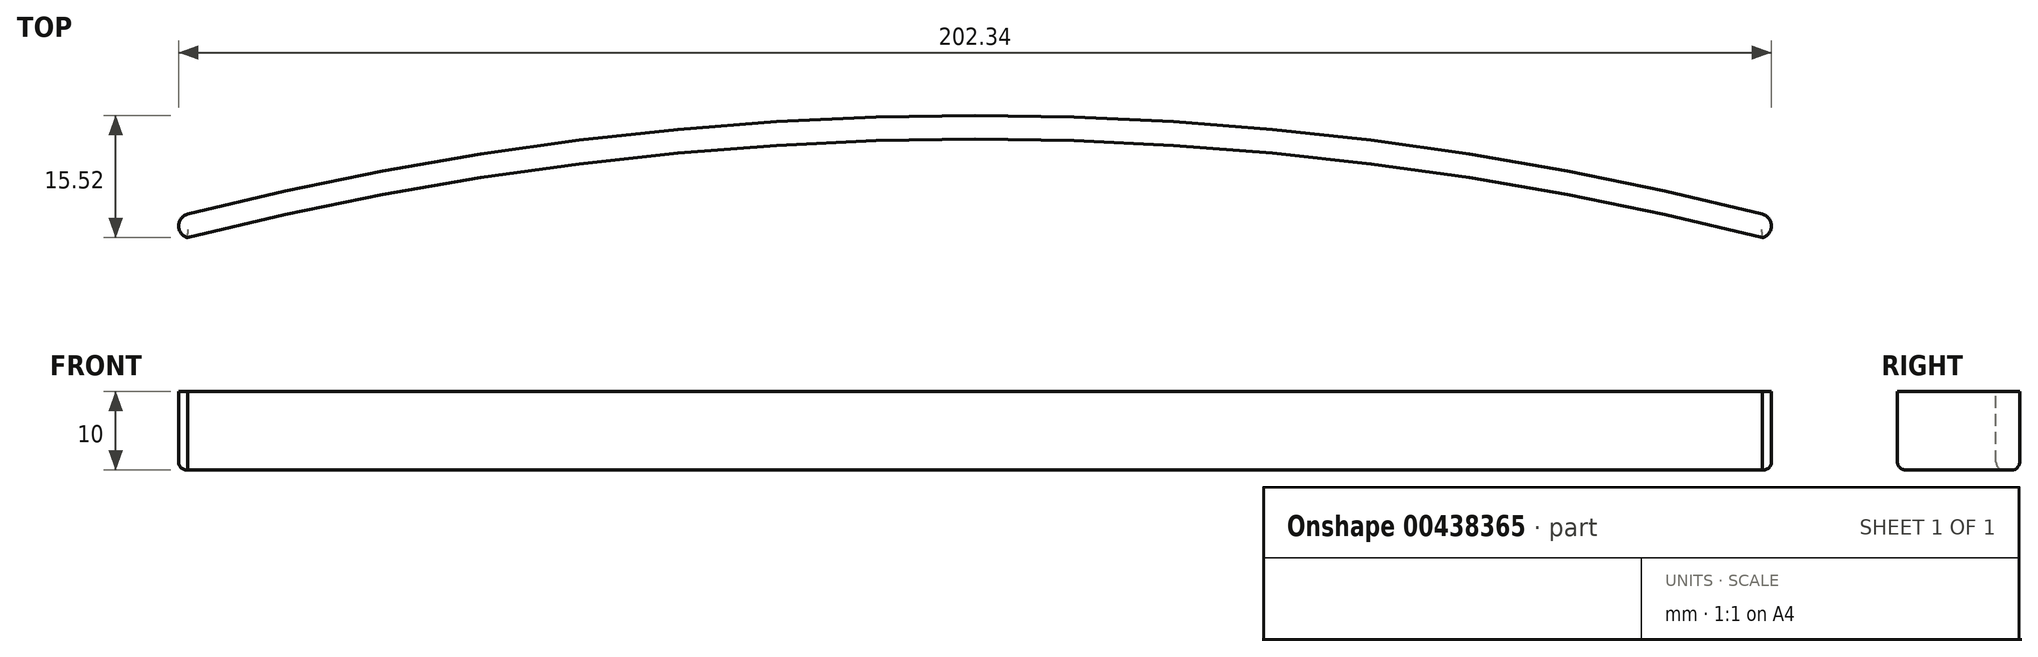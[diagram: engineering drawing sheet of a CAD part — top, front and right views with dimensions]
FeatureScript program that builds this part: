
annotation { "Feature Type Name" : "Feature", "Feature Type Description" : "" }
export const myFeature = defineFeature(function(context is Context, id is Id, definition is map)
    precondition{}
    {
        {
            var Q0;
            Q0=qCreatedBy(makeId("Top.planeOp"),FACE);
            var sketch = newSketch(context, id + "F0", { "sketchPlane" : qUnion([Q0])});
            skArc(sketch, "E0", {"start": v(100, -5.67) * mm, "mid": v(0, 6.85) * mm, "end": v(-100, -5.67) * mm});
            skArc(sketch, "E1", {"start": v(100, -2.67) * mm, "mid": v(0, 9.85) * mm, "end": v(-100, -2.67) * mm});
            skArc(sketch, "E2", {"start": v(-100, -2.67) * mm, "mid": v(-101.17, -4.17) * mm, "end": v(-100, -5.67) * mm});
            skArc(sketch, "E3", {"start": v(100, -2.67) * mm, "mid": v(101.17, -4.17) * mm, "end": v(100, -5.67) * mm});
            skSolve(sketch);
        }
        {
            var Q0;
            Q0=makeQuery(id+"F0.imprint","IMPRINT",FACE,{"disambiguationData":[TD([[makeQuery(id+"F0.imprint","IMPRINT",EDGE,{"derivedFrom":sQuery(id+"F0.wireOp",EDGE,"E0")}),-1.0]])]});
            extrude(context, id + "F1", {"entities" : qUnion([Q0]), "oppositeDirection" : true, "depth" : 10 * mm});
        }
        {
            var Q0;
            Q0=makeQuery(id+"F1.opExtrude","CAP_EDGE",EDGE,{"disambiguationData":[OSD([sQuery(id+"F0.wireOp",EDGE,"E0")])],"isStart":false});
            var Q1;
            Q1=makeQuery(id+"F1.opExtrude","CAP_EDGE",EDGE,{"disambiguationData":[OSD([sQuery(id+"F0.wireOp",EDGE,"E3")])],"isStart":false});
            fillet(context, id + "F2", {"entities" : qUnion([Q0, Q1]), "radius" : 1 * mm, "tangentPropagation" : true, "allowEdgeOverflow" : false});
        }
    });
